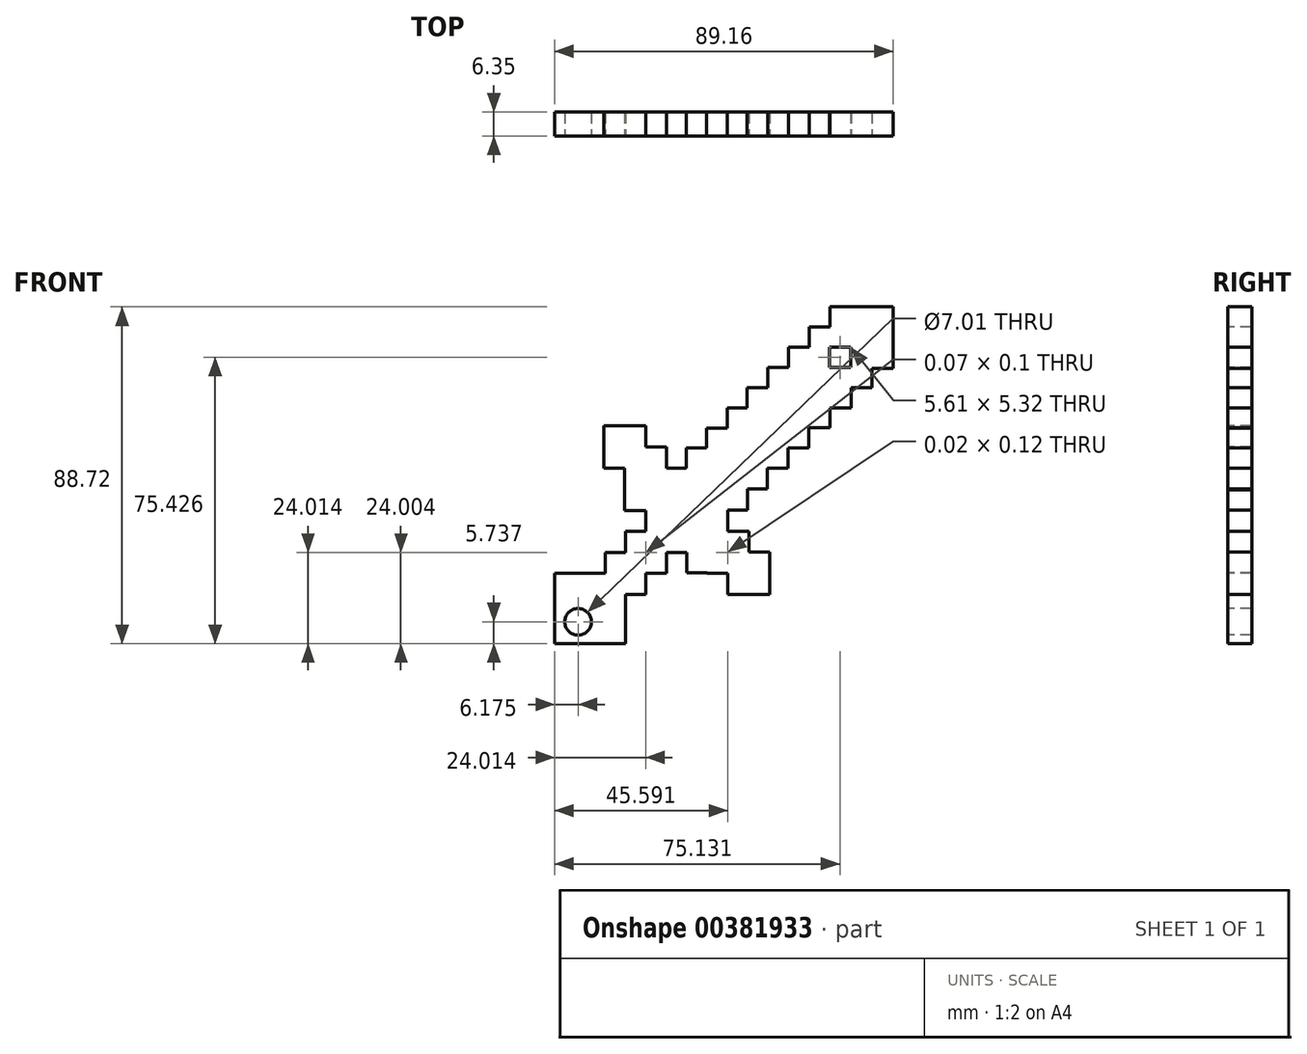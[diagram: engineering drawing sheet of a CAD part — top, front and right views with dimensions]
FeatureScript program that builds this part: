
annotation { "Feature Type Name" : "Feature", "Feature Type Description" : "" }
export const myFeature = defineFeature(function(context is Context, id is Id, definition is map)
    precondition{}
    {
        {
            var Q0;
            Q0=qCreatedBy(makeId("Front.planeOp"),FACE);
            var sketch = newSketch(context, id + "F0", { "sketchPlane" : qUnion([Q0])});
            skLineSegment(sketch, "E0.bottom", {"start": v(-54.91, -24.94) * mm, "end": v(-36.22, -24.94) * mm});
            skLineSegment(sketch, "E0.top", {"start": v(-54.91, -43.46) * mm, "end": v(-36.22, -43.46) * mm});
            skLineSegment(sketch, "E0.left", {"start": v(-54.91, -24.94) * mm, "end": v(-54.91, -43.46) * mm});
            skLineSegment(sketch, "E0.right", {"start": v(-36.22, -24.94) * mm, "end": v(-36.22, -43.46) * mm});
            skPoint(sketch, "E1", {"position": v(-45.57, -34.2) * mm});
            skPoint(sketch, "E2.orphan", {"position": v(-45.57, -24.94) * mm});
            skPoint(sketch, "E3.orphan", {"position": v(-36.22, -34.2) * mm});
            skPoint(sketch, "E4.end.orphan", {"position": v(-45.57, -43.46) * mm});
            skPoint(sketch, "E5.start.orphan", {"position": v(-54.91, -34.2) * mm});
            skLineSegment(sketch, "E6.bottom", {"start": v(-41.62, -37.8) * mm, "end": v(-49.52, -37.8) * mm});
            skLineSegment(sketch, "E6.top", {"start": v(-41.62, -30.6) * mm, "end": v(-49.52, -30.6) * mm});
            skLineSegment(sketch, "E6.left", {"start": v(-41.62, -37.8) * mm, "end": v(-41.62, -30.6) * mm});
            skLineSegment(sketch, "E6.right", {"start": v(-49.52, -37.8) * mm, "end": v(-49.52, -30.6) * mm});
            skLineSegment(sketch, "E7.bottom", {"start": v(-30.86, -19.4) * mm, "end": v(-41.59, -19.4) * mm});
            skLineSegment(sketch, "E7.top", {"start": v(-30.86, -30.48) * mm, "end": v(-41.59, -30.48) * mm});
            skLineSegment(sketch, "E7.left", {"start": v(-30.86, -19.4) * mm, "end": v(-30.86, -30.48) * mm});
            skLineSegment(sketch, "E7.right", {"start": v(-41.59, -19.4) * mm, "end": v(-41.59, -30.48) * mm});
            skPoint(sketch, "E7.middle", {"position": v(-36.22, -24.94) * mm});
            skLineSegment(sketch, "E8.bottom", {"start": v(-25.5, -24.94) * mm, "end": v(-36.22, -24.94) * mm});
            skLineSegment(sketch, "E8.top", {"start": v(-25.5, -13.87) * mm, "end": v(-36.22, -13.87) * mm});
            skLineSegment(sketch, "E8.left", {"start": v(-25.5, -24.94) * mm, "end": v(-25.5, -13.87) * mm});
            skLineSegment(sketch, "E8.right", {"start": v(-36.22, -24.94) * mm, "end": v(-36.22, -13.87) * mm});
            skPoint(sketch, "E8.middle", {"position": v(-30.86, -19.4) * mm});
            skLineSegment(sketch, "E9.bottom", {"start": v(-20.13, -8.39) * mm, "end": v(-30.93, -8.39) * mm});
            skLineSegment(sketch, "E9.left", {"start": v(-20.13, -8.39) * mm, "end": v(-20.13, -19.35) * mm});
            skPoint(sketch, "E9.middle", {"position": v(-25.5, -13.87) * mm});
            skLineSegment(sketch, "E10.bottom", {"start": v(-14.86, -13.87) * mm, "end": v(-25.5, -13.87) * mm});
            skLineSegment(sketch, "E10.top", {"start": v(-14.86, -2.91) * mm, "end": v(-20.23, -2.91) * mm});
            skLineSegment(sketch, "E10.left", {"start": v(-14.86, -8.39) * mm, "end": v(-14.86, -2.91) * mm});
            skLineSegment(sketch, "E10.right", {"start": v(-25.4, -13.87) * mm, "end": v(-25.4, -2.91) * mm});
            skPoint(sketch, "E10.middle", {"position": v(-20.13, -8.39) * mm});
            skLineSegment(sketch, "E11.bottom", {"start": v(-9.5, -8.39) * mm, "end": v(-20.23, -8.39) * mm});
            skLineSegment(sketch, "E11.right", {"start": v(-20.23, -8.39) * mm, "end": v(-20.23, 2.73) * mm});
            skPoint(sketch, "E11.middle", {"position": v(-14.86, -2.91) * mm});
            skPoint(sketch, "E11.cornerSnap0", {"position": v(-14.86, -8.39) * mm});
            skPoint(sketch, "E12.middle", {"position": v(-9.5, 2.57) * mm});
            skLineSegment(sketch, "E13.bottom", {"start": v(-4.16, -2.9) * mm, "end": v(-14.84, -2.9) * mm});
            skLineSegment(sketch, "E13.top", {"start": v(-4.16, 8.04) * mm, "end": v(-14.84, 8.04) * mm});
            skLineSegment(sketch, "E13.left", {"start": v(-4.16, -2.9) * mm, "end": v(-4.16, 8.04) * mm});
            skLineSegment(sketch, "E13.right", {"start": v(-14.84, -2.9) * mm, "end": v(-14.84, 8.04) * mm});
            skLineSegment(sketch, "E14.bottom", {"start": v(1.16, 2.73) * mm, "end": v(-9.49, 2.73) * mm});
            skLineSegment(sketch, "E14.top", {"start": v(1.16, 13.36) * mm, "end": v(-9.49, 13.36) * mm});
            skLineSegment(sketch, "E14.left", {"start": v(1.16, 2.73) * mm, "end": v(1.16, 13.36) * mm});
            skLineSegment(sketch, "E14.right", {"start": v(-9.49, 2.73) * mm, "end": v(-9.49, 13.36) * mm});
            skPoint(sketch, "E14.middle", {"position": v(-4.16, 8.04) * mm});
            skLineSegment(sketch, "E15.bottom", {"start": v(6.6, 8.04) * mm, "end": v(-4.28, 8.04) * mm});
            skLineSegment(sketch, "E15.top", {"start": v(6.6, 18.68) * mm, "end": v(-4.28, 18.68) * mm});
            skLineSegment(sketch, "E15.left", {"start": v(6.6, 8.04) * mm, "end": v(6.6, 18.68) * mm});
            skLineSegment(sketch, "E15.right", {"start": v(-4.28, 8.04) * mm, "end": v(-4.28, 18.68) * mm});
            skPoint(sketch, "E15.middle", {"position": v(1.16, 13.36) * mm});
            skPoint(sketch, "E15.cornerSnap0", {"position": v(1.16, 8.04) * mm});
            skLineSegment(sketch, "E16.bottom", {"start": v(12.14, 13.36) * mm, "end": v(1.06, 13.36) * mm});
            skLineSegment(sketch, "E16.top", {"start": v(12.14, 24) * mm, "end": v(1.06, 24) * mm});
            skLineSegment(sketch, "E16.left", {"start": v(12.14, 13.36) * mm, "end": v(12.14, 24) * mm});
            skLineSegment(sketch, "E16.right", {"start": v(1.06, 13.36) * mm, "end": v(1.06, 24) * mm});
            skPoint(sketch, "E16.middle", {"position": v(6.6, 18.68) * mm});
            skLineSegment(sketch, "E17.bottom", {"start": v(17.58, 18.68) * mm, "end": v(6.7, 18.68) * mm});
            skLineSegment(sketch, "E17.top", {"start": v(17.58, 29.3) * mm, "end": v(6.7, 29.3) * mm});
            skLineSegment(sketch, "E17.left", {"start": v(17.58, 18.68) * mm, "end": v(17.58, 29.3) * mm});
            skLineSegment(sketch, "E17.right", {"start": v(6.7, 18.68) * mm, "end": v(6.7, 29.3) * mm});
            skPoint(sketch, "E17.middle", {"position": v(12.14, 24) * mm});
            skLineSegment(sketch, "E18.bottom", {"start": v(23.03, 24) * mm, "end": v(12.14, 24) * mm});
            skLineSegment(sketch, "E18.top", {"start": v(23.03, 34.62) * mm, "end": v(12.14, 34.62) * mm});
            skLineSegment(sketch, "E18.left", {"start": v(23.03, 24) * mm, "end": v(23.03, 34.62) * mm});
            skLineSegment(sketch, "E18.right", {"start": v(12.14, 24) * mm, "end": v(12.14, 34.62) * mm});
            skPoint(sketch, "E18.middle", {"position": v(17.58, 29.3) * mm});
            skLineSegment(sketch, "E19.bottom", {"start": v(28.63, 29.3) * mm, "end": v(17.42, 29.3) * mm});
            skLineSegment(sketch, "E19.top", {"start": v(28.63, 39.94) * mm, "end": v(17.42, 39.94) * mm});
            skLineSegment(sketch, "E19.left", {"start": v(28.63, 29.3) * mm, "end": v(28.63, 39.94) * mm});
            skLineSegment(sketch, "E19.right", {"start": v(17.42, 29.3) * mm, "end": v(17.42, 39.94) * mm});
            skPoint(sketch, "E19.middle", {"position": v(23.03, 34.62) * mm});
            skLineSegment(sketch, "E20.bottom", {"start": v(28.63, 34.62) * mm, "end": v(23.04, 34.62) * mm});
            skLineSegment(sketch, "E20.top", {"start": v(34.23, 45.26) * mm, "end": v(23.04, 45.26) * mm});
            skLineSegment(sketch, "E20.left", {"start": v(34.23, 34.62) * mm, "end": v(34.23, 45.26) * mm});
            skLineSegment(sketch, "E20.right", {"start": v(23.04, 34.62) * mm, "end": v(23.04, 39.94) * mm});
            skPoint(sketch, "E20.middle", {"position": v(28.63, 39.94) * mm});
            skLineSegment(sketch, "E21.bottom", {"start": v(-30.93, 2.73) * mm, "end": v(-9.33, 2.73) * mm});
            skLineSegment(sketch, "E21.top", {"start": v(-30.93, -19.5) * mm, "end": v(-9.33, -19.5) * mm});
            skLineSegment(sketch, "E21.left", {"start": v(-30.93, 2.73) * mm, "end": v(-30.93, -19.5) * mm});
            skLineSegment(sketch, "E21.right", {"start": v(-9.33, 2.73) * mm, "end": v(-9.33, -19.5) * mm});
            skLineSegment(sketch, "E22", {"start": v(-25.4, -2.91) * mm, "end": v(-25.4, 2.73) * mm});
            skLineSegment(sketch, "E23", {"start": v(-14.86, -13.87) * mm, "end": v(-9.33, -13.87) * mm});
            skLineSegment(sketch, "E24.MirrorCS", {"start": v(-36.47, -2.91) * mm, "end": v(-36.47, 2.73) * mm});
            skLineSegment(sketch, "E25.MirrorCS", {"start": v(-30.93, 2.73) * mm, "end": v(-36.47, 2.73) * mm});
            skLineSegment(sketch, "E26.MirrorCS", {"start": v(-36.47, -8.39) * mm, "end": v(-30.93, -8.39) * mm});
            skLineSegment(sketch, "E27.MirrorCS", {"start": v(-36.47, -8.39) * mm, "end": v(-36.47, -2.91) * mm});
            skPoint(sketch, "E28.orphan", {"position": v(-36.47, -13.87) * mm});
            skPoint(sketch, "E29.orphan", {"position": v(-41.73, -8.39) * mm});
            skPoint(sketch, "E30.orphan", {"position": v(-52.54, 2.73) * mm});
            skLineSegment(sketch, "E31.top", {"start": v(-25.4, 8.37) * mm, "end": v(-36.47, 8.37) * mm});
            skLineSegment(sketch, "E31.left", {"start": v(-25.4, -2.91) * mm, "end": v(-25.4, 8.37) * mm});
            skLineSegment(sketch, "E31.right", {"start": v(-36.47, -2.91) * mm, "end": v(-36.47, 8.37) * mm});
            skPoint(sketch, "E31.middle", {"position": v(-30.93, 2.73) * mm});
            skLineSegment(sketch, "E32.bottom", {"start": v(-30.93, 2.73) * mm, "end": v(-42, 2.73) * mm});
            skLineSegment(sketch, "E32.top", {"start": v(-30.93, 14) * mm, "end": v(-42, 14) * mm});
            skLineSegment(sketch, "E32.left", {"start": v(-30.93, 2.73) * mm, "end": v(-30.93, 14) * mm});
            skLineSegment(sketch, "E32.right", {"start": v(-42, 2.73) * mm, "end": v(-42, 14) * mm});
            skPoint(sketch, "E32.middle", {"position": v(-36.47, 8.37) * mm});
            skPoint(sketch, "E33.orphan", {"position": v(-31, -8.39) * mm});
            skPoint(sketch, "E34.orphan", {"position": v(-30.86, -8.39) * mm});
            skPoint(sketch, "E35.orphan", {"position": v(-30.86, -19.35) * mm});
            skLineSegment(sketch, "E36.bottom", {"start": v(-14.84, -24.85) * mm, "end": v(-20.13, -24.85) * mm});
            skLineSegment(sketch, "E36.left", {"start": v(-14.84, -19.5) * mm, "end": v(-14.84, -13.85) * mm});
            skPoint(sketch, "E36.middle", {"position": v(-20.13, -19.35) * mm});
            skLineSegment(sketch, "E37", {"start": v(-20.13, -19.35) * mm, "end": v(-20.13, -24.85) * mm});
            skLineSegment(sketch, "E38.bottom", {"start": v(-14.84, -19.5) * mm, "end": v(-9.3, -19.5) * mm});
            skLineSegment(sketch, "E38.top", {"start": v(-14.84, -24.92) * mm, "end": v(-9.3, -24.92) * mm});
            skLineSegment(sketch, "E38.left", {"start": v(-14.84, -24.85) * mm, "end": v(-14.84, -24.92) * mm});
            skLineSegment(sketch, "E38.right", {"start": v(-9.3, -19.5) * mm, "end": v(-9.3, -24.92) * mm});
            skLineSegment(sketch, "E39.bottom", {"start": v(-9.33, -13.87) * mm, "end": v(-3.78, -13.87) * mm});
            skLineSegment(sketch, "E39.top", {"start": v(-9.33, -19.39) * mm, "end": v(-3.78, -19.39) * mm});
            skLineSegment(sketch, "E39.left", {"start": v(-9.33, -13.87) * mm, "end": v(-9.33, -19.39) * mm});
            skLineSegment(sketch, "E39.right", {"start": v(-3.78, -13.87) * mm, "end": v(-3.78, -19.39) * mm});
            skLineSegment(sketch, "E40.bottom", {"start": v(-3.78, -19.39) * mm, "end": v(-9.3, -19.39) * mm});
            skLineSegment(sketch, "E40.top", {"start": v(-3.78, -24.92) * mm, "end": v(-9.3, -24.92) * mm});
            skLineSegment(sketch, "E40.left", {"start": v(-3.78, -19.39) * mm, "end": v(-3.78, -24.92) * mm});
            skLineSegment(sketch, "E40.right", {"start": v(-9.3, -19.39) * mm, "end": v(-9.3, -24.92) * mm});
            skPoint(sketch, "E41.orphan", {"position": v(0, -13.87) * mm});
            skLineSegment(sketch, "E42.bottom", {"start": v(1.76, -30.45) * mm, "end": v(-9.3, -30.45) * mm});
            skLineSegment(sketch, "E42.top", {"start": v(1.76, -19.39) * mm, "end": v(-9.3, -19.39) * mm});
            skLineSegment(sketch, "E42.left", {"start": v(1.76, -30.45) * mm, "end": v(1.76, -19.39) * mm});
            skLineSegment(sketch, "E42.right", {"start": v(-9.3, -30.45) * mm, "end": v(-9.3, -19.39) * mm});
            skPoint(sketch, "E42.middle", {"position": v(-3.78, -24.92) * mm});
            skLineSegment(sketch, "E43.bottom", {"start": v(-9.5, 8.04) * mm, "end": v(-14.92, 8.04) * mm});
            skLineSegment(sketch, "E43.top", {"start": v(-9.49, 13.36) * mm, "end": v(-14.92, 13.36) * mm});
            skLineSegment(sketch, "E43.right", {"start": v(-14.92, 8.04) * mm, "end": v(-14.92, 13.36) * mm});
            skPoint(sketch, "E44.firstSnap0", {"position": v(-14.84, 2.57) * mm});
            skLineSegment(sketch, "E44.bottom", {"start": v(-14.84, 2.73) * mm, "end": v(-20.27, 2.73) * mm});
            skLineSegment(sketch, "E44.top", {"start": v(-14.84, 8.07) * mm, "end": v(-20.27, 8.07) * mm});
            skLineSegment(sketch, "E44.left", {"start": v(-14.84, 2.73) * mm, "end": v(-14.84, 8.07) * mm});
            skLineSegment(sketch, "E44.right", {"start": v(-20.27, 2.73) * mm, "end": v(-20.27, 8.07) * mm});
            skLineSegment(sketch, "E45.bottom", {"start": v(-4.16, 13.36) * mm, "end": v(-9.49, 13.36) * mm});
            skLineSegment(sketch, "E45.top", {"start": v(-4.16, 18.64) * mm, "end": v(-9.49, 18.64) * mm});
            skLineSegment(sketch, "E45.right", {"start": v(-9.49, 13.36) * mm, "end": v(-9.49, 18.64) * mm});
            skLineSegment(sketch, "E46.bottom", {"start": v(1.16, 18.68) * mm, "end": v(-4.2, 18.68) * mm});
            skLineSegment(sketch, "E46.top", {"start": v(1.16, 24) * mm, "end": v(-4.2, 24) * mm});
            skLineSegment(sketch, "E46.left", {"start": v(1.16, 24) * mm, "end": v(1.16, 24) * mm});
            skLineSegment(sketch, "E46.right", {"start": v(-4.2, 18.68) * mm, "end": v(-4.2, 24) * mm});
            skLineSegment(sketch, "E47.bottom", {"start": v(-9.33, -2.9) * mm, "end": v(-4.05, -2.9) * mm});
            skLineSegment(sketch, "E47.top", {"start": v(-9.33, -8.3) * mm, "end": v(-4.05, -8.3) * mm});
            skLineSegment(sketch, "E47.left", {"start": v(-9.33, -2.9) * mm, "end": v(-9.33, -8.3) * mm});
            skLineSegment(sketch, "E47.right", {"start": v(-4.05, -2.9) * mm, "end": v(-4.05, -8.3) * mm});
            skLineSegment(sketch, "E48.bottom", {"start": v(-4.16, 2.73) * mm, "end": v(1.13, 2.73) * mm});
            skLineSegment(sketch, "E48.top", {"start": v(-4.16, -2.74) * mm, "end": v(1.13, -2.74) * mm});
            skLineSegment(sketch, "E48.left", {"start": v(-4.16, 2.73) * mm, "end": v(-4.16, -2.74) * mm});
            skLineSegment(sketch, "E48.right", {"start": v(1.13, 2.73) * mm, "end": v(1.13, -2.74) * mm});
            skLineSegment(sketch, "E49.bottom", {"start": v(1.16, 8.04) * mm, "end": v(6.61, 8.04) * mm});
            skLineSegment(sketch, "E49.top", {"start": v(1.16, 2.74) * mm, "end": v(6.61, 2.74) * mm});
            skLineSegment(sketch, "E49.left", {"start": v(1.16, 8.04) * mm, "end": v(1.16, 2.74) * mm});
            skLineSegment(sketch, "E49.right", {"start": v(6.61, 8.04) * mm, "end": v(6.61, 2.74) * mm});
            skLineSegment(sketch, "E50.bottom", {"start": v(6.7, 24) * mm, "end": v(1.16, 24) * mm});
            skLineSegment(sketch, "E50.top", {"start": v(6.7, 29.28) * mm, "end": v(1.16, 29.28) * mm});
            skLineSegment(sketch, "E50.left", {"start": v(6.7, 24) * mm, "end": v(6.7, 29.28) * mm});
            skLineSegment(sketch, "E50.right", {"start": v(1.16, 24) * mm, "end": v(1.16, 29.28) * mm});
            skLineSegment(sketch, "E51.bottom", {"start": v(12.14, 29.3) * mm, "end": v(6.7, 29.3) * mm});
            skLineSegment(sketch, "E51.top", {"start": v(12.14, 34.67) * mm, "end": v(6.7, 34.67) * mm});
            skLineSegment(sketch, "E51.left", {"start": v(12.14, 29.3) * mm, "end": v(12.14, 34.67) * mm});
            skLineSegment(sketch, "E51.right", {"start": v(6.7, 29.3) * mm, "end": v(6.7, 34.67) * mm});
            skPoint(sketch, "E52.firstSnap0", {"position": v(6.6, 13.36) * mm});
            skLineSegment(sketch, "E52.bottom", {"start": v(6.7, 13.36) * mm, "end": v(12.06, 13.36) * mm});
            skLineSegment(sketch, "E52.top", {"start": v(6.61, 8.04) * mm, "end": v(12.06, 8.04) * mm});
            skLineSegment(sketch, "E52.right", {"start": v(12.06, 13.36) * mm, "end": v(12.06, 8.04) * mm});
            skLineSegment(sketch, "E53.bottom", {"start": v(12.14, 18.68) * mm, "end": v(17.58, 18.68) * mm});
            skLineSegment(sketch, "E53.top", {"start": v(12.14, 13.39) * mm, "end": v(17.58, 13.39) * mm});
            skLineSegment(sketch, "E53.left", {"start": v(12.14, 18.68) * mm, "end": v(12.14, 13.39) * mm});
            skLineSegment(sketch, "E53.right", {"start": v(17.58, 18.68) * mm, "end": v(17.58, 13.39) * mm});
            skLineSegment(sketch, "E54.bottom", {"start": v(17.58, 24) * mm, "end": v(23.15, 24) * mm});
            skLineSegment(sketch, "E54.top", {"start": v(17.58, 18.68) * mm, "end": v(23.15, 18.68) * mm});
            skLineSegment(sketch, "E54.left", {"start": v(17.58, 24) * mm, "end": v(17.58, 18.68) * mm});
            skLineSegment(sketch, "E54.right", {"start": v(23.15, 24) * mm, "end": v(23.15, 18.68) * mm});
            skLineSegment(sketch, "E55.bottom", {"start": v(23.03, 29.3) * mm, "end": v(28.65, 29.3) * mm});
            skLineSegment(sketch, "E55.top", {"start": v(23.03, 23.98) * mm, "end": v(28.65, 23.98) * mm});
            skLineSegment(sketch, "E55.left", {"start": v(23.03, 29.3) * mm, "end": v(23.03, 23.98) * mm});
            skLineSegment(sketch, "E55.right", {"start": v(28.65, 29.3) * mm, "end": v(28.65, 23.98) * mm});
            skLineSegment(sketch, "E56.bottom", {"start": v(34.23, 34.62) * mm, "end": v(34.25, 34.62) * mm});
            skLineSegment(sketch, "E56.top", {"start": v(28.63, 29.08) * mm, "end": v(34.25, 29.08) * mm});
            skLineSegment(sketch, "E56.left", {"start": v(28.63, 34.62) * mm, "end": v(28.63, 29.08) * mm});
            skLineSegment(sketch, "E56.right", {"start": v(34.25, 34.62) * mm, "end": v(34.25, 29.08) * mm});
            skLineSegment(sketch, "E57.bottom", {"start": v(17.42, 34.62) * mm, "end": v(12.14, 34.62) * mm});
            skLineSegment(sketch, "E57.top", {"start": v(17.42, 39.97) * mm, "end": v(12.14, 39.97) * mm});
            skLineSegment(sketch, "E57.left", {"start": v(17.42, 34.62) * mm, "end": v(17.42, 39.97) * mm});
            skLineSegment(sketch, "E57.right", {"start": v(12.14, 34.62) * mm, "end": v(12.14, 39.97) * mm});
            skLineSegment(sketch, "E58.bottom", {"start": v(23.04, 39.94) * mm, "end": v(17.58, 39.94) * mm});
            skLineSegment(sketch, "E58.top", {"start": v(23.04, 45.26) * mm, "end": v(17.58, 45.26) * mm});
            skLineSegment(sketch, "E58.right", {"start": v(17.58, 39.94) * mm, "end": v(17.58, 45.26) * mm});
            skLineSegment(sketch, "E59.bottom", {"start": v(28.63, 39.94) * mm, "end": v(34.23, 39.94) * mm});
            skLineSegment(sketch, "E59.top", {"start": v(28.63, 45.26) * mm, "end": v(34.23, 45.26) * mm});
            skLineSegment(sketch, "E59.left", {"start": v(28.63, 39.94) * mm, "end": v(28.63, 45.26) * mm});
            skLineSegment(sketch, "E59.right", {"start": v(34.23, 39.94) * mm, "end": v(34.23, 45.26) * mm});
            skPoint(sketch, "E60.orphan", {"position": v(-25.42, -24.85) * mm});
            skPoint(sketch, "E61.trimOffspring.end.orphan", {"position": v(-25.42, -13.85) * mm});
            skPoint(sketch, "E62.orphan", {"position": v(-20.23, 2.57) * mm});
            skSolve(sketch);
        }
        {
            var Q0;
            Q0=qSketchRegion(id+"F0",true);
            var Q1;
            {var subQ0=sQuery(id+"F0.wireOp",EDGE,"E10.right");var subQ1=sQuery(id+"F0.wireOp",EDGE,"E10.bottom");var subQ2=makeQuery(id+"F0.imprint","INTERSECT",VERTEX,{"derivedFrom":[subQ1,subQ0]});Q1=makeQuery(id+"F0.imprint","IMPRINT",FACE,{"disambiguationData":[TD([[makeQuery(id+"F0.imprint","IMPRINT",EDGE,{"disambiguationData":[TD([[subQ2,1.0]])],"derivedFrom":subQ1}),1.0]])]});}
            var Q2;
            {var subQ0=sQuery(id+"F0.wireOp",EDGE,"E11.bottom");var subQ3=sQuery(id+"F0.wireOp",EDGE,"E9.left");var subQ4=makeQuery(id+"F0.imprint","INTERSECT",VERTEX,{"derivedFrom":[subQ3,subQ0]});Q2=makeQuery(id+"F0.imprint","IMPRINT",FACE,{"disambiguationData":[TD([[makeQuery(id+"F0.imprint","IMPRINT",EDGE,{"disambiguationData":[TD([[subQ4,-1.0]])],"derivedFrom":subQ3}),-1.0]])]});}
            var Q3;
            Q3=makeQuery(id+"F0.imprint","IMPRINT",FACE,{"disambiguationData":[TD([[makeQuery(id+"F0.imprint","IMPRINT",EDGE,{"derivedFrom":sQuery(id+"F0.wireOp",EDGE,"E6.bottom")}),-1.0]])]});
            var Q4;
            {var subQ11=sQuery(id+"F0.wireOp",EDGE,"E10.top");Q4=makeQuery(id+"F0.imprint","IMPRINT",FACE,{"disambiguationData":[TD([[makeQuery(id+"F0.imprint","IMPRINT",EDGE,{"derivedFrom":subQ11}),-1.0]])]});}
            var Q5;
            {var subQ5=sQuery(id+"F0.wireOp",EDGE,"E10.top");Q5=makeQuery(id+"F0.imprint","IMPRINT",FACE,{"disambiguationData":[TD([[makeQuery(id+"F0.imprint","IMPRINT",EDGE,{"derivedFrom":subQ5}),1.0]])]});}
            var Q6;
            {var subQ0=sQuery(id+"F0.wireOp",EDGE,"E11.left");var subQ1=sQuery(id+"F0.wireOp",EDGE,"E11.top");var subQ2=makeQuery(id+"F0.imprint","INTERSECT",VERTEX,{"derivedFrom":[subQ1,subQ0]});Q6=makeQuery(id+"F0.imprint","IMPRINT",FACE,{"disambiguationData":[TD([[makeQuery(id+"F0.imprint","IMPRINT",EDGE,{"disambiguationData":[TD([[subQ2,-1.0]])],"derivedFrom":subQ1}),1.0]])]});}
            var Q7;
            {var subQ5=sQuery(id+"F0.wireOp",EDGE,"E14.top");Q7=makeQuery(id+"F0.imprint","IMPRINT",FACE,{"disambiguationData":[TD([[makeQuery(id+"F0.imprint","IMPRINT",EDGE,{"derivedFrom":subQ5}),1.0]])]});}
            var Q8;
            {var subQ5=sQuery(id+"F0.wireOp",EDGE,"E17.bottom");Q8=makeQuery(id+"F0.imprint","IMPRINT",FACE,{"disambiguationData":[TD([[makeQuery(id+"F0.imprint","IMPRINT",EDGE,{"derivedFrom":subQ5}),-1.0]])]});}
            var Q9;
            {var subQ1=sQuery(id+"F0.wireOp",EDGE,"E17.top");Q9=makeQuery(id+"F0.imprint","IMPRINT",FACE,{"disambiguationData":[TD([[makeQuery(id+"F0.imprint","IMPRINT",EDGE,{"derivedFrom":subQ1}),1.0]])]});}
            var Q10;
            Q10=makeQuery(id+"F0.imprint","IMPRINT",FACE,{"disambiguationData":[TD([[makeQuery(id+"F0.imprint","IMPRINT",EDGE,{"derivedFrom":sQuery(id+"F0.wireOp",EDGE,"E17.top")}),-1.0]])]});
            var Q11;
            Q11=makeQuery(id+"F0.imprint","IMPRINT",FACE,{"disambiguationData":[TD([[makeQuery(id+"F0.imprint","IMPRINT",EDGE,{"derivedFrom":sQuery(id+"F0.wireOp",EDGE,"E18.top")}),1.0]])]});
            var Q12;
            {var subQ0=sQuery(id+"F0.wireOp",EDGE,"E17.left");Q12=makeQuery(id+"F0.imprint","IMPRINT",FACE,{"disambiguationData":[TD([[makeQuery(id+"F0.imprint","IMPRINT",EDGE,{"derivedFrom":subQ0}),-1.0]])]});}
            var Q13;
            {var subQ0=sQuery(id+"F0.wireOp",EDGE,"E19.left");Q13=makeQuery(id+"F0.imprint","IMPRINT",FACE,{"disambiguationData":[TD([[makeQuery(id+"F0.imprint","IMPRINT",EDGE,{"derivedFrom":subQ0}),1.0]])]});}
            var Q14;
            {var subQ5=sQuery(id+"F0.wireOp",EDGE,"E13.bottom");Q14=makeQuery(id+"F0.imprint","IMPRINT",FACE,{"disambiguationData":[TD([[makeQuery(id+"F0.imprint","IMPRINT",EDGE,{"derivedFrom":subQ5}),-1.0]])]});}
            var Q15;
            {var subQ0=sQuery(id+"F0.wireOp",EDGE,"E43.bottom");var subQ1=sQuery(id+"F0.wireOp",EDGE,"E13.top");var subQ2=makeQuery(id+"F0.imprint","INTERSECT",VERTEX,{"derivedFrom":[subQ1,subQ0]});Q15=makeQuery(id+"F0.imprint","IMPRINT",FACE,{"disambiguationData":[TD([[makeQuery(id+"F0.imprint","IMPRINT",EDGE,{"disambiguationData":[TD([[subQ2,1.0]])],"derivedFrom":subQ1}),1.0]])]});}
            var Q16;
            {var subQ0=sQuery(id+"F0.wireOp",EDGE,"E21.bottom");var subQ7=sQuery(id+"F0.wireOp",EDGE,"E14.right");var subQ8=makeQuery(id+"F0.imprint","INTERSECT",VERTEX,{"derivedFrom":[subQ7,subQ0]});Q16=makeQuery(id+"F0.imprint","IMPRINT",FACE,{"disambiguationData":[TD([[makeQuery(id+"F0.imprint","IMPRINT",EDGE,{"disambiguationData":[TD([[subQ8,-1.0]])],"derivedFrom":subQ7}),-1.0]])]});}
            var Q17;
            {var subQ2=sQuery(id+"F0.wireOp",EDGE,"E15.left");var subQ4=sQuery(id+"F0.wireOp",EDGE,"E15.top");var subQ5=makeQuery(id+"F0.imprint","INTERSECT",VERTEX,{"derivedFrom":[subQ4,subQ2]});Q17=makeQuery(id+"F0.imprint","IMPRINT",FACE,{"disambiguationData":[TD([[makeQuery(id+"F0.imprint","IMPRINT",EDGE,{"disambiguationData":[TD([[subQ5,-1.0]])],"derivedFrom":subQ4}),1.0]])]});}
            var Q18;
            {var subQ3=sQuery(id+"F0.wireOp",EDGE,"E49.bottom");var subQ5=sQuery(id+"F0.wireOp",EDGE,"E15.left");var subQ6=makeQuery(id+"F0.imprint","INTERSECT",VERTEX,{"derivedFrom":[subQ5,subQ3]});Q18=makeQuery(id+"F0.imprint","IMPRINT",FACE,{"disambiguationData":[TD([[makeQuery(id+"F0.imprint","IMPRINT",EDGE,{"disambiguationData":[TD([[subQ6,-1.0]])],"derivedFrom":subQ5}),1.0]])]});}
            extrude(context, id + "F1", {"entities" : qUnion([Q0, Q1, Q2, Q3, Q4, Q5, Q6, Q7, Q8, Q9, Q10, Q11, Q12, Q13, Q14, Q15, Q16, Q17, Q18]), "oppositeDirection" : true, "depth" : 6.35 * mm});
        }
        {
            var Q0;
            Q0=qCreatedBy(makeId("Front.planeOp"),FACE);
            var sketch = newSketch(context, id + "F2", { "sketchPlane" : qUnion([Q0])});
            skCircle(sketch, "E63", {"center": v(-48.73, -37.72) * mm, "radius": 3.5 * mm});
            skSolve(sketch);
        }
        {
            var Q0;
            Q0=qSketchRegion(id+"F2",true);
            extrude(context, id + "F3", {"entities" : qUnion([Q0]), "operationType" : NewBodyOperationType.REMOVE, "oppositeDirection" : true, "depth" : 6.35 * mm});
        }
    });
